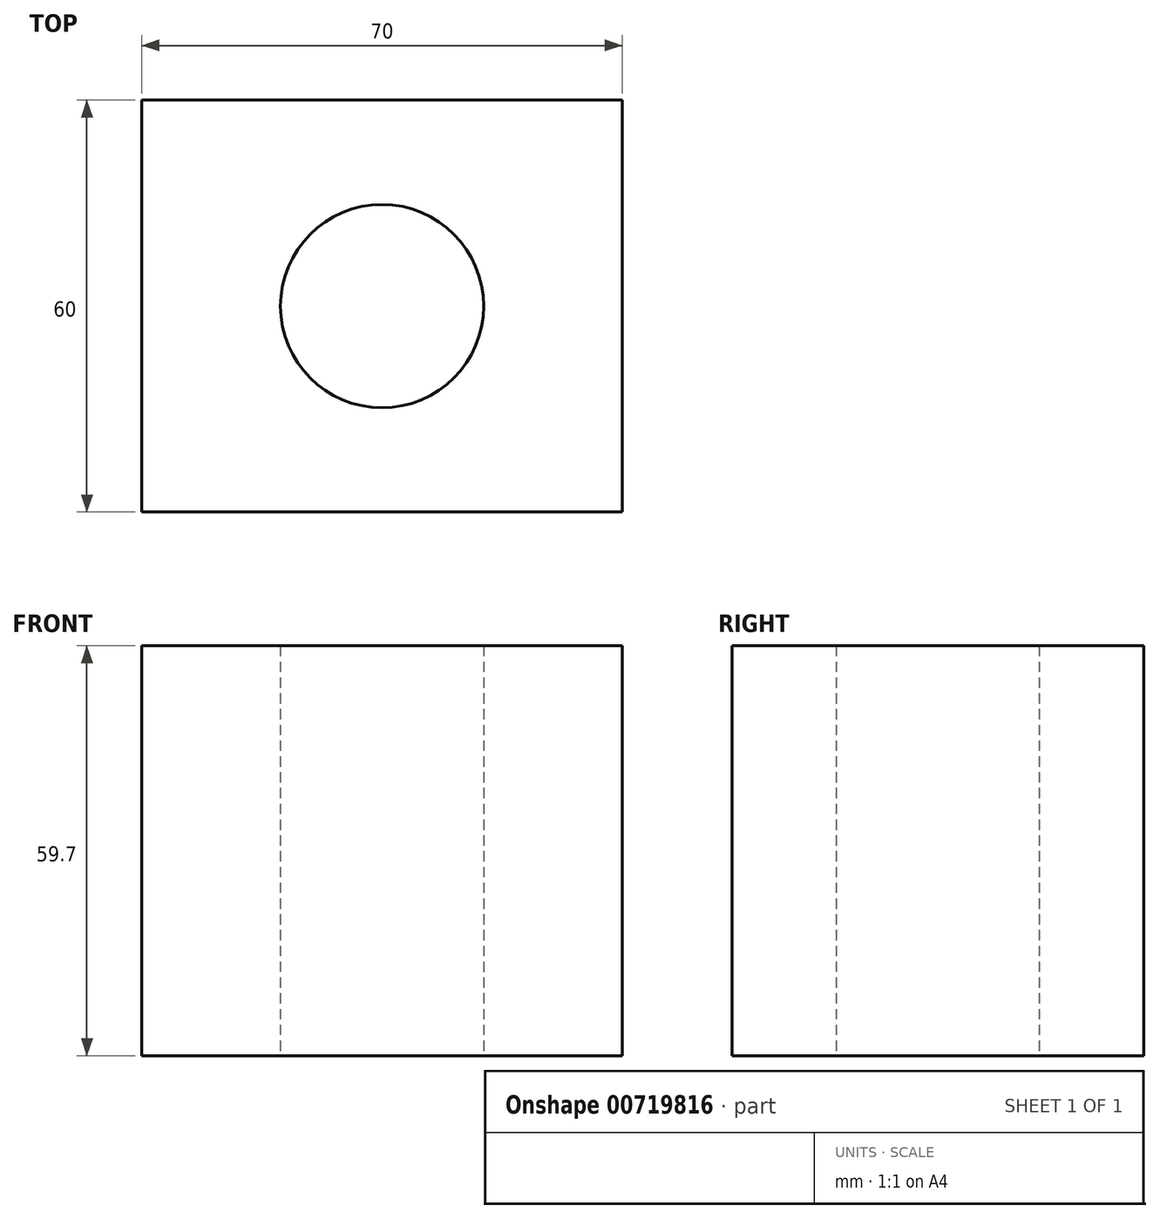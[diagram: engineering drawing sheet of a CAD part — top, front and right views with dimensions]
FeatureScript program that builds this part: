
annotation { "Feature Type Name" : "Feature", "Feature Type Description" : "" }
export const myFeature = defineFeature(function(context is Context, id is Id, definition is map)
    precondition{}
    {
        {
            var Q0;
            Q0=qCreatedBy(makeId("Top.planeOp"),FACE);
            var sketch = newSketch(context, id + "F0", { "sketchPlane" : qUnion([Q0])});
            skLineSegment(sketch, "E0.bottom", {"start": v(35, -30) * mm, "end": v(-35, -30) * mm});
            skLineSegment(sketch, "E0.top", {"start": v(35, 30) * mm, "end": v(-35, 30) * mm});
            skLineSegment(sketch, "E0.left", {"start": v(35, -30) * mm, "end": v(35, 30) * mm});
            skLineSegment(sketch, "E0.right", {"start": v(-35, -30) * mm, "end": v(-35, 30) * mm});
            skPoint(sketch, "E0.middle", {"position": v(0, 0) * mm});
            skCircle(sketch, "E1", {"center": v(0, 0) * mm, "radius": 14.8 * mm});
            skSolve(sketch);
        }
        {
            var Q0;
            Q0 = qSketchRegion(id + "F0", true);
            extrude(context, id + "F1", {"entities" : qUnion([Q0]), "depth" : 59.7 * mm, "offsetDistance" : 25 * mm});
        }
    });
